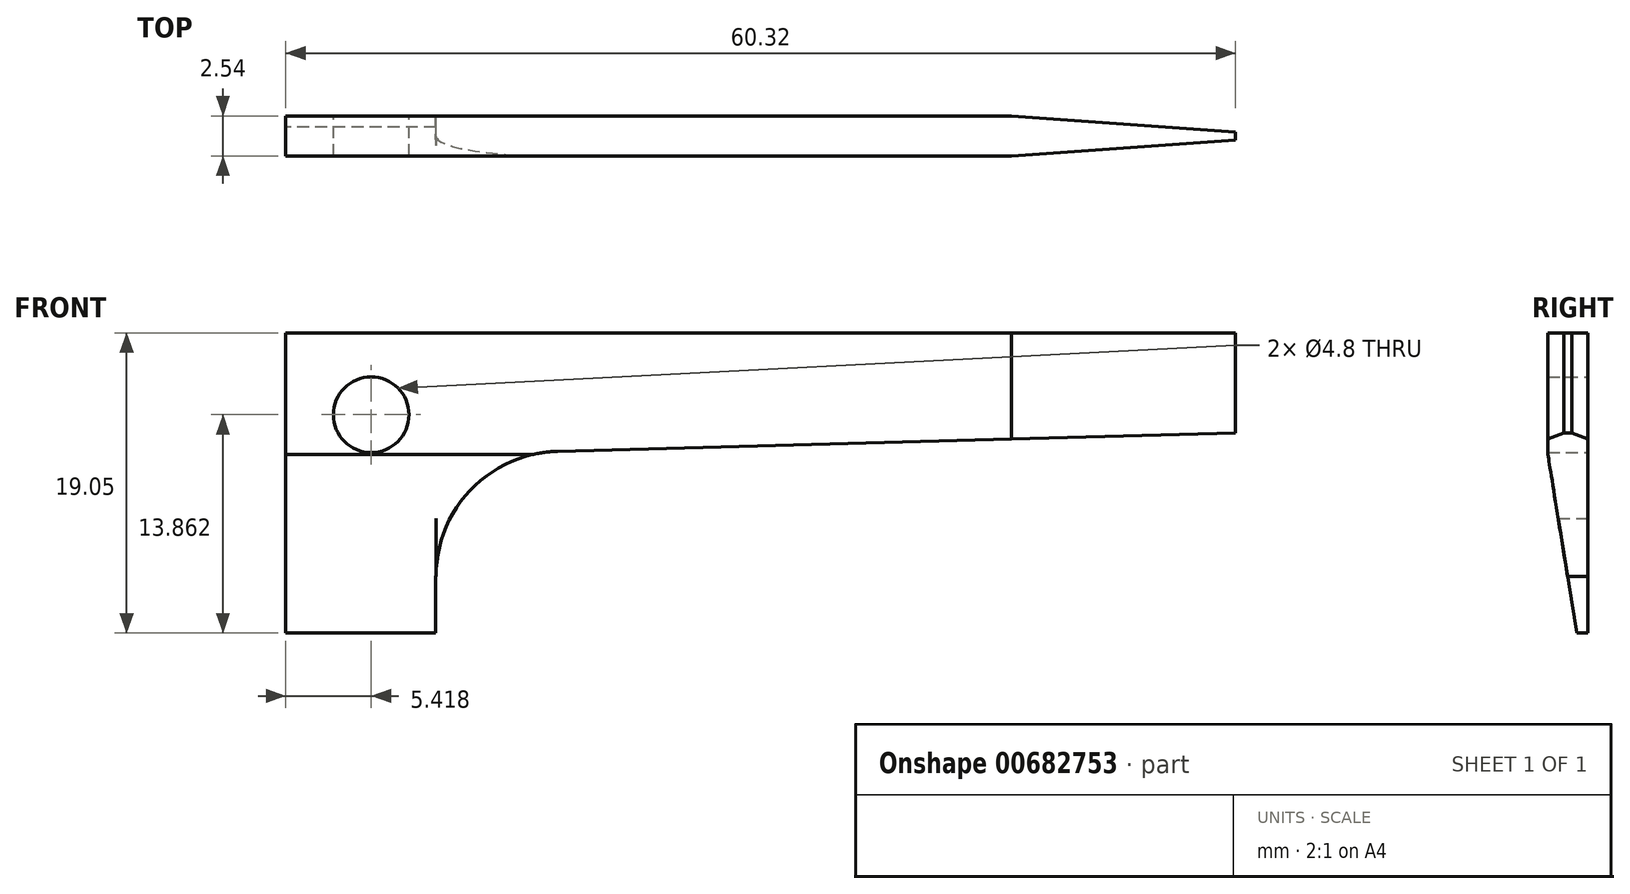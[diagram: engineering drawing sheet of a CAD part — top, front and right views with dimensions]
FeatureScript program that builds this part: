
annotation { "Feature Type Name" : "Feature", "Feature Type Description" : "" }
export const myFeature = defineFeature(function(context is Context, id is Id, definition is map)
    precondition{}
    {
        {
            var Q0;
            Q0=qCreatedBy(makeId("Front.planeOp"),FACE);
            var sketch = newSketch(context, id + "F0", { "sketchPlane" : qUnion([Q0])});
            skLineSegment(sketch, "E0.bottom", {"start": v(-9.53, 7.72) * mm, "end": v(50.8, 7.72) * mm});
            skLineSegment(sketch, "E0.top", {"start": v(-9.53, -11.33) * mm, "end": v(0, -11.33) * mm});
            skLineSegment(sketch, "E0.left", {"start": v(-9.53, 7.72) * mm, "end": v(-9.53, -11.33) * mm});
            skLineSegment(sketch, "E0.right", {"start": v(50.8, 7.72) * mm, "end": v(50.8, 1.37) * mm});
            skPoint(sketch, "E1.visualSharp", {"position": v(4.1, 4) * mm});
            skLineSegment(sketch, "E2", {"start": v(0, -11.33) * mm, "end": v(0, -3.2) * mm});
            skPoint(sketch, "E3.start.orphan", {"position": v(11.25, 4) * mm});
            skLineSegment(sketch, "E4", {"start": v(50.8, 1.37) * mm, "end": v(7.72, 0.2) * mm});
            skLineSegment(sketch, "E5", {"start": v(0, -4.05) * mm, "end": v(0, -7.72) * mm});
            skPoint(sketch, "E6.visualSharp", {"position": v(0, 0) * mm});
            skArc(sketch, "E6.filletArc", {"start": v(7.72, 0.2) * mm, "mid": v(2.25, -2.19) * mm, "end": v(0, -7.72) * mm});
            skCircle(sketch, "E7", {"center": v(-4.11, 2.53) * mm, "radius": 2.4 * mm});
            skSolve(sketch);
        }
        {
            var Q0;
            Q0 = qSketchRegion(id + "F0", true);
            extrude(context, id + "F1", {"entities" : qUnion([Q0]), "depth" : 2.54 * mm, "offsetDistance" : 25.4 * mm});
        }
        {
            var Q0;
            Q0=makeQuery(id+"F1.opExtrude","SWEPT_FACE",FACE,{"disambiguationData":[OSD([sQuery(id+"F0.wireOp",EDGE,"E0.left")])]});
            var sketch = newSketch(context, id + "F2", { "sketchPlane" : qUnion([Q0])});
            skLineSegment(sketch, "E8", {"start": v(2.54, 0) * mm, "end": v(0.72, -11.33) * mm});
            skLineSegment(sketch, "E9", {"start": v(0.72, -11.33) * mm, "end": v(2.54, -11.33) * mm});
            skLineSegment(sketch, "E10", {"start": v(2.54, -11.33) * mm, "end": v(2.54, 0) * mm});
            skSolve(sketch);
        }
        {
            var Q0;
            Q0 = qSketchRegion(id + "F2", true);
            extrude(context, id + "F3", {"entities" : qUnion([Q0]), "operationType" : NewBodyOperationType.REMOVE, "oppositeDirection" : true, "depth" : 25.4 * mm, "offsetDistance" : 25.4 * mm});
        }
        {
            var Q0;
            Q0=makeQuery(id+"F1.opExtrude","SWEPT_FACE",FACE,{"disambiguationData":[OSD([sQuery(id+"F0.wireOp",EDGE,"E0.bottom")])]});
            var sketch = newSketch(context, id + "F4", { "sketchPlane" : qUnion([Q0])});
            skLineSegment(sketch, "E11", {"start": v(36.56, 1.07) * mm, "end": v(36.56, -6.33) * mm});
            skLineSegment(sketch, "E12", {"start": v(36.56, 0) * mm, "end": v(50.8, -1.02) * mm});
            skLineSegment(sketch, "E13", {"start": v(50.8, -1.02) * mm, "end": v(50.8, -1.52) * mm});
            skLineSegment(sketch, "E14", {"start": v(50.8, -1.52) * mm, "end": v(36.56, -2.54) * mm});
            skLineSegment(sketch, "E15", {"start": v(36.56, 0) * mm, "end": v(50.8, 0) * mm});
            skLineSegment(sketch, "E16", {"start": v(50.8, 0) * mm, "end": v(50.8, -1.02) * mm});
            skLineSegment(sketch, "E17", {"start": v(50.8, -1.52) * mm, "end": v(50.8, -2.54) * mm});
            skLineSegment(sketch, "E18", {"start": v(50.8, -2.54) * mm, "end": v(36.56, -2.54) * mm});
            skSolve(sketch);
        }
        {
            var Q0;
            Q0=makeQuery(id+"F4.imprint","IMPRINT",FACE,{"disambiguationData":[TD([[makeQuery(id+"F4.imprint","IMPRINT",EDGE,{"derivedFrom":sQuery(id+"F4.wireOp",EDGE,"E12")}),1.0]])]});
            var Q1;
            Q1=makeQuery(id+"F4.imprint","IMPRINT",FACE,{"disambiguationData":[TD([[makeQuery(id+"F4.imprint","IMPRINT",EDGE,{"derivedFrom":sQuery(id+"F4.wireOp",EDGE,"E14")}),1.0]])]});
            extrude(context, id + "F5", {"entities" : qUnion([Q0, Q1]), "operationType" : NewBodyOperationType.REMOVE, "oppositeDirection" : true, "depth" : 25.4 * mm, "offsetDistance" : 25.4 * mm});
        }
    });
